# Revit family: ASSA_ABLOY_DockLeveler_DL6220T
name_source: partatom
category: Specialty Equipment
units: mm (PartAtom-declared; Revit-internal decimal feet)

## family parameters
Always vertical = Yes
Cut with Voids When Loaded = No
Enable Cutting in Views = No
Host = Floor
Maintain Annotation Orientation = No
Part Type = Normal
Room Calculation Point = No
Round Connector Dimension = Use Diameter
Shared = No

## types (3) — shared parameters
DL6220T_LipLL1000 = DL6220T_Platform : DL6220T_LipLL1000
DL6220T_LipLL500 = DL6220T_Platform : DL6220T_LipLL500
Description = Dock Leveler
FloorThickness = 1250 mm  [stored 4.10105 ft]
Manufacturer = ASSA ABLOY
Model = DL6220T
TailLiftWidth = 3000 mm  [stored 9.84252 ft]
zero-valued in all types: Default Elevation

## per-type parameters (varying)
| type | LipLength | LipType | URL |
| Lip LL1000 | 1000 mm  [stored 3.28084 ft] | DL6220T_Platform : DL6220T_LipLL1000 | https://www.assaabloyentrance.com |
| Lip LL500 | 500 mm  [stored 1.64042 ft] | DL6220T_Platform : DL6220T_LipLL500 |  |
| Lip ErgoLL345 | 345 mm  [stored 1.13189 ft] | DL6220T_Platform : DL6220T_LipLL500 |  |

note: [stored X ft] marks values corroborated as IEEE doubles in the binary element streams (Revit-internal decimal feet)

## geometry (parser evidence)
native form markers: Sweep x31
no freeform markers — native parametric forms only
